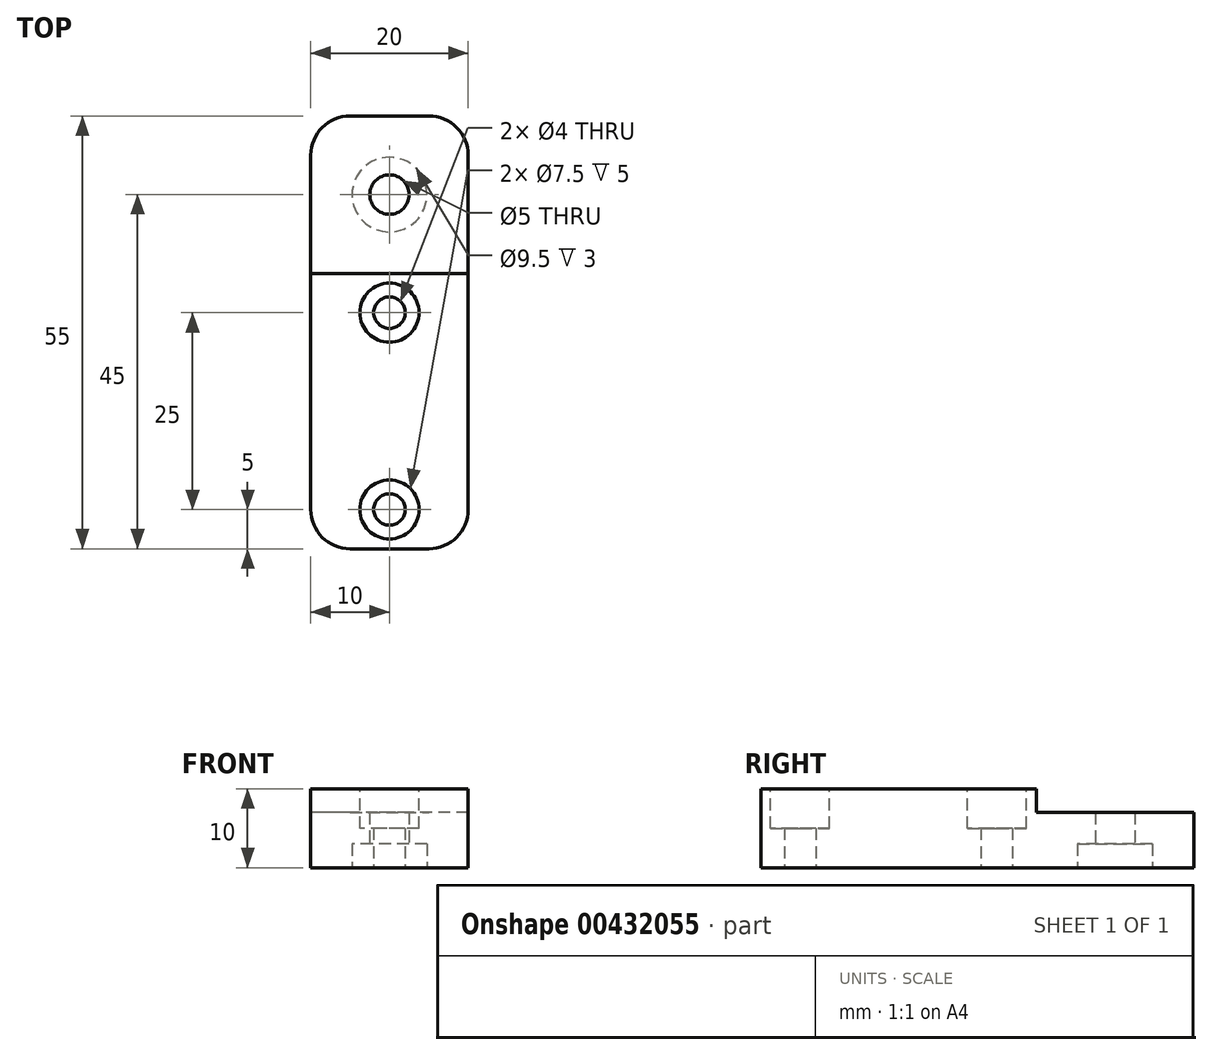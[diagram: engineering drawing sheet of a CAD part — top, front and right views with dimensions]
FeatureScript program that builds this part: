
annotation { "Feature Type Name" : "Feature", "Feature Type Description" : "" }
export const myFeature = defineFeature(function(context is Context, id is Id, definition is map)
    precondition{}
    {
        {
            var Q0;
            Q0=qCreatedBy(makeId("Top.planeOp"),FACE);
            var sketch = newSketch(context, id + "F0", { "sketchPlane" : qUnion([Q0])});
            skLineSegment(sketch, "E0.bottom", {"start": v(0, 0) * mm, "end": v(20, 0) * mm});
            skLineSegment(sketch, "E0.top", {"start": v(0, 55) * mm, "end": v(20, 55) * mm});
            skLineSegment(sketch, "E0.left", {"start": v(0, 0) * mm, "end": v(0, 55) * mm});
            skLineSegment(sketch, "E0.right", {"start": v(20, 0) * mm, "end": v(20, 55) * mm});
            skCircle(sketch, "E1", {"center": v(10, 5) * mm, "radius": 2 * mm});
            skPoint(sketch, "E1.centerSnap0", {"position": v(10, 0) * mm});
            skCircle(sketch, "E2", {"center": v(10, 30) * mm, "radius": 2 * mm});
            skCircle(sketch, "E3", {"center": v(10, 45) * mm, "radius": 2.5 * mm});
            skPoint(sketch, "E3.centerSnap0", {"position": v(10, 55) * mm});
            skSolve(sketch);
        }
        {
            var Q0;
            Q0=makeQuery(id+"F0.imprint","IMPRINT",FACE,{"disambiguationData":[TD([[makeQuery(id+"F0.imprint","IMPRINT",EDGE,{"derivedFrom":sQuery(id+"F0.wireOp",EDGE,"E0.bottom")}),1.0]])]});
            extrude(context, id + "F1", {"entities" : qUnion([Q0]), "depth" : 10 * mm});
        }
        {
            var Q0;
            Q0=makeQuery(id+"F1.opExtrude","CAP_FACE",FACE,{"disambiguationData":[OSD([sQuery(id+"F0.wireOp",EDGE,"E0.bottom"),sQuery(id+"F0.wireOp",EDGE,"E0.top"),sQuery(id+"F0.wireOp",EDGE,"E0.left"),sQuery(id+"F0.wireOp",EDGE,"E0.right"),sQuery(id+"F0.wireOp",EDGE,"E1"),sQuery(id+"F0.wireOp",EDGE,"E2"),sQuery(id+"F0.wireOp",EDGE,"E3")])],"isStart":false});
            var sketch = newSketch(context, id + "F2", { "sketchPlane" : qUnion([Q0])});
            skCircle(sketch, "E4", {"center": v(10, 5) * mm, "radius": 3.75 * mm});
            skCircle(sketch, "E5", {"center": v(10, 30) * mm, "radius": 3.75 * mm});
            skSolve(sketch);
        }
        {
            var Q0;
            Q0=qSketchRegion(id+"F2",true);
            extrude(context, id + "F3", {"entities" : qUnion([Q0]), "operationType" : NewBodyOperationType.REMOVE, "oppositeDirection" : true, "depth" : 5 * mm});
        }
        {
            var Q0;
            Q0=makeQuery(id+"F1.opExtrude","CAP_FACE",FACE,{"disambiguationData":[OSD([sQuery(id+"F0.wireOp",EDGE,"E0.bottom"),sQuery(id+"F0.wireOp",EDGE,"E0.top"),sQuery(id+"F0.wireOp",EDGE,"E0.left"),sQuery(id+"F0.wireOp",EDGE,"E0.right"),sQuery(id+"F0.wireOp",EDGE,"E1"),sQuery(id+"F0.wireOp",EDGE,"E2"),sQuery(id+"F0.wireOp",EDGE,"E3")])],"isStart":false});
            var sketch = newSketch(context, id + "F4", { "sketchPlane" : qUnion([Q0])});
            skLineSegment(sketch, "E6", {"start": v(20, 35) * mm, "end": v(0, 35) * mm});
            skSolve(sketch);
        }
        {
            var Q0;
            Q0=qSketchRegion(id+"F4",true);
            var Q1;
            {var subQ2=sQuery(id+"F4.wireOp",EDGE,"E6");Q1=makeQuery(id+"F4.imprint","IMPRINT",FACE,{"disambiguationData":[TD([[makeQuery(id+"F4.imprint","IMPRINT",EDGE,{"derivedFrom":subQ2}),-1.0]])]});}
            extrude(context, id + "F5", {"entities" : qUnion([Q0, Q1]), "operationType" : NewBodyOperationType.REMOVE, "oppositeDirection" : true, "depth" : 3 * mm});
        }
        {
            var Q0;
            Q0=makeQuery(id+"F1.opExtrude","SWEPT_EDGE",EDGE,{"disambiguationData":[OSD([sQuery(id+"F0.wireOp",EDGE,"E0.bottom"),sQuery(id+"F0.wireOp",EDGE,"E0.right")])]});
            var Q1;
            Q1=makeQuery(id+"F1.opExtrude","SWEPT_EDGE",EDGE,{"disambiguationData":[OSD([sQuery(id+"F0.wireOp",EDGE,"E0.top"),sQuery(id+"F0.wireOp",EDGE,"E0.right")])]});
            var Q2;
            Q2=makeQuery(id+"F1.opExtrude","SWEPT_EDGE",EDGE,{"disambiguationData":[OSD([sQuery(id+"F0.wireOp",EDGE,"E0.top"),sQuery(id+"F0.wireOp",EDGE,"E0.left")])]});
            var Q3;
            Q3=makeQuery(id+"F1.opExtrude","SWEPT_EDGE",EDGE,{"disambiguationData":[OSD([sQuery(id+"F0.wireOp",EDGE,"E0.bottom"),sQuery(id+"F0.wireOp",EDGE,"E0.left")])]});
            var Q4;
            Q4=makeQuery(id+"F5.boolean.opBoolean","COPY",EDGE,{"derivedFrom":makeQuery(id+"F5.opExtrude","SWEPT_EDGE",EDGE,{"disambiguationData":[OSD([sQuery(id+"F0.wireOp",EDGE,"E0.right"),sQuery(id+"F4.wireOp",EDGE,"E6")])]})});
            var Q5;
            Q5=makeQuery(id+"F5.boolean.opBoolean","COPY",EDGE,{"derivedFrom":makeQuery(id+"F5.opExtrude","SWEPT_EDGE",EDGE,{"disambiguationData":[OSD([sQuery(id+"F0.wireOp",EDGE,"E0.left"),sQuery(id+"F4.wireOp",EDGE,"E6")])]})});
            fillet(context, id + "F6", {"entities" : qUnion([Q0, Q1, Q2, Q3, Q4, Q5]), "radius" : 5 * mm, "tangentPropagation" : true, "allowEdgeOverflow" : false});
        }
        {
            var Q0;
            Q0=makeQuery(id+"F0.imprint","IMPRINT",FACE,{"disambiguationData":[TD([[makeQuery(id+"F0.imprint","IMPRINT",EDGE,{"derivedFrom":sQuery(id+"F0.wireOp",EDGE,"E0.bottom")}),1.0]])]});
            var sketch = newSketch(context, id + "F7", { "sketchPlane" : qUnion([Q0])});
            skCircle(sketch, "E7", {"center": v(10, 45) * mm, "radius": 4.75 * mm});
            skSolve(sketch);
        }
        {
            var Q0;
            Q0=makeQuery(id+"F7.imprint","IMPRINT",FACE,{"disambiguationData":[TD([[makeQuery(id+"F7.imprint","IMPRINT",EDGE,{"derivedFrom":sQuery(id+"F7.wireOp",EDGE,"E7")}),1.0]])]});
            extrude(context, id + "F8", {"entities" : qUnion([Q0]), "operationType" : NewBodyOperationType.REMOVE, "depth" : 3 * mm});
        }
    });
